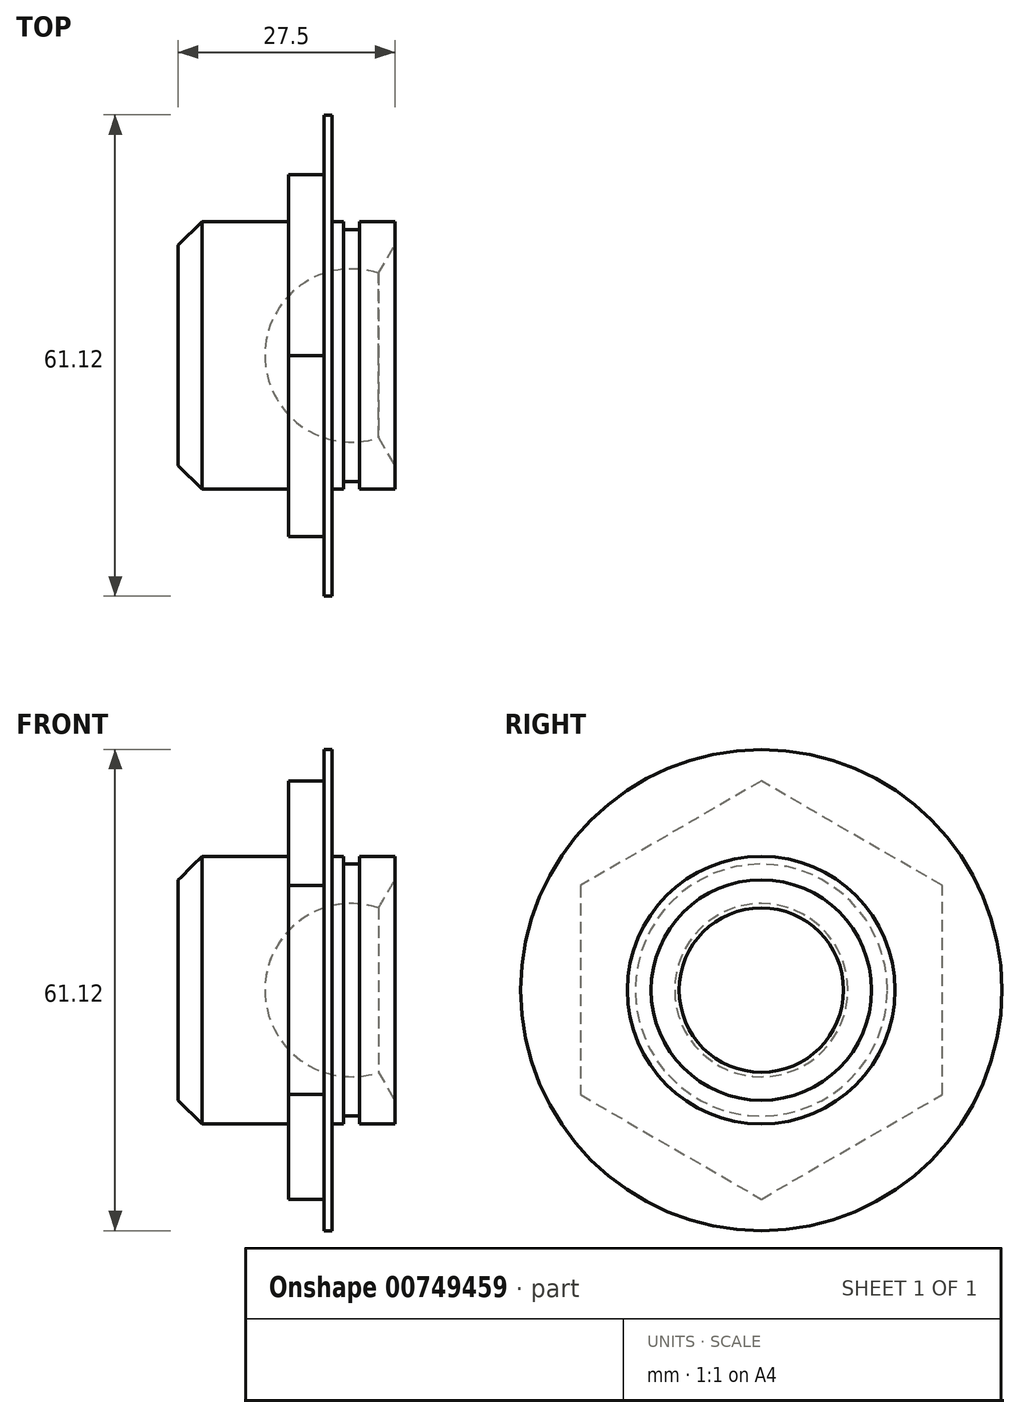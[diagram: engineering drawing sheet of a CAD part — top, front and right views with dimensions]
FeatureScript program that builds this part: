
annotation { "Feature Type Name" : "Feature", "Feature Type Description" : "" }
export const myFeature = defineFeature(function(context is Context, id is Id, definition is map)
    precondition{}
    {
        {
            var Q0;
            Q0=qCreatedBy(makeId("Front.planeOp"),FACE);
            var sketch = newSketch(context, id + "F0", { "sketchPlane" : qUnion([Q0])});
            skLineSegment(sketch, "E0", {"start": v(0, 0) * mm, "end": v(22, 0) * mm, "construction": true});
            skLineSegment(sketch, "E1", {"start": v(0, 0) * mm, "end": v(0, 17) * mm});
            skLineSegment(sketch, "E2", {"start": v(0, 17) * mm, "end": v(14, 17) * mm});
            skLineSegment(sketch, "E3", {"start": v(14, 17) * mm, "end": v(14, 40) * mm});
            skLineSegment(sketch, "E4", {"start": v(14, 40) * mm, "end": v(18.5, 40) * mm});
            skLineSegment(sketch, "E5", {"start": v(18.5, 40) * mm, "end": v(18.5, 17) * mm});
            skLineSegment(sketch, "E6", {"start": v(18.5, 17) * mm, "end": v(21, 17) * mm});
            skArc(sketch, "E7", {"start": v(25.45, 10.45) * mm, "mid": v(15.56, 8.91) * mm, "end": v(11, 0) * mm});
            skLineSegment(sketch, "E8", {"start": v(25.45, 10.45) * mm, "end": v(27.5, 14) * mm});
            skLineSegment(sketch, "E9", {"start": v(27.5, 17) * mm, "end": v(27.5, 14) * mm});
            skLineSegment(sketch, "E10", {"start": v(0, 0) * mm, "end": v(11, 0) * mm});
            skLineSegment(sketch, "E11", {"start": v(23, 17) * mm, "end": v(23, 16) * mm});
            skLineSegment(sketch, "E12", {"start": v(23, 16) * mm, "end": v(21, 16) * mm});
            skLineSegment(sketch, "E13", {"start": v(21, 16) * mm, "end": v(21, 17) * mm});
            skLineSegment(sketch, "E14.trimOffspring", {"start": v(23, 17) * mm, "end": v(27.5, 17) * mm});
            skSolve(sketch);
        }
        {
            var Q0;
            Q0=makeQuery(id+"F0.imprint","IMPRINT",FACE,{"disambiguationData":[TD([[makeQuery(id+"F0.imprint","IMPRINT",EDGE,{"derivedFrom":sQuery(id+"F0.wireOp",EDGE,"E1")}),-1.0]])]});
            var Q1;
            Q1=sQuery(id+"F0.wireOp",EDGE,"E0");
            revolve(context, id + "F1", {"surfaceOperationType" : NewSurfaceOperationType.NEW, "entities" : qUnion([Q0]), "axis" : qUnion([Q1]), "revolveType" : RevolveType.FULL});
        }
        {
            var Q0;
            Q0=makeQuery(id+"F1.opRevolve","SWEPT_FACE",FACE,{"disambiguationData":[OSD([sQuery(id+"F0.wireOp",EDGE,"E3")])]});
            var sketch = newSketch(context, id + "F2", { "sketchPlane" : qUnion([Q0])});
            skLineSegment(sketch, "E15.bottom", {"start": v(23, -47.62) * mm, "end": v(64.72, -47.62) * mm});
            skLineSegment(sketch, "E15.top", {"start": v(23, 47.62) * mm, "end": v(64.72, 47.62) * mm});
            skLineSegment(sketch, "E15.left", {"start": v(23, -47.62) * mm, "end": v(23, 47.62) * mm});
            skLineSegment(sketch, "E15.right", {"start": v(64.72, -47.62) * mm, "end": v(64.72, 47.62) * mm});
            skPoint(sketch, "E15.middle", {"position": v(43.86, 0) * mm});
            skLineSegment(sketch, "E16.1.0", {"start": v(52.74, -3.89) * mm, "end": v(73.6, 32.24) * mm});
            skLineSegment(sketch, "E16.1.1", {"start": v(52.74, -3.89) * mm, "end": v(-29.74, 43.73) * mm});
            skLineSegment(sketch, "E16.1.2", {"start": v(-29.74, 43.73) * mm, "end": v(-8.88, 79.86) * mm});
            skLineSegment(sketch, "E16.1.3", {"start": v(73.6, 32.24) * mm, "end": v(-8.88, 79.86) * mm});
            skLineSegment(sketch, "E16.2.0", {"start": v(29.74, 43.73) * mm, "end": v(8.88, 79.86) * mm});
            skLineSegment(sketch, "E16.2.1", {"start": v(29.74, 43.73) * mm, "end": v(-52.74, -3.89) * mm});
            skLineSegment(sketch, "E16.2.2", {"start": v(-52.74, -3.89) * mm, "end": v(-73.6, 32.24) * mm});
            skLineSegment(sketch, "E16.2.3", {"start": v(8.88, 79.86) * mm, "end": v(-73.6, 32.24) * mm});
            skLineSegment(sketch, "E16.3.0", {"start": v(-23, 47.62) * mm, "end": v(-64.72, 47.62) * mm});
            skLineSegment(sketch, "E16.3.1", {"start": v(-23, 47.62) * mm, "end": v(-23, -47.62) * mm});
            skLineSegment(sketch, "E16.3.2", {"start": v(-23, -47.62) * mm, "end": v(-64.72, -47.62) * mm});
            skLineSegment(sketch, "E16.3.3", {"start": v(-64.72, 47.62) * mm, "end": v(-64.72, -47.62) * mm});
            skLineSegment(sketch, "E16.4.0", {"start": v(-52.74, 3.89) * mm, "end": v(-73.6, -32.24) * mm});
            skLineSegment(sketch, "E16.4.1", {"start": v(-52.74, 3.89) * mm, "end": v(29.74, -43.73) * mm});
            skLineSegment(sketch, "E16.4.2", {"start": v(29.74, -43.73) * mm, "end": v(8.88, -79.86) * mm});
            skLineSegment(sketch, "E16.4.3", {"start": v(-73.6, -32.24) * mm, "end": v(8.88, -79.86) * mm});
            skLineSegment(sketch, "E16.5.0", {"start": v(-29.74, -43.73) * mm, "end": v(-8.88, -79.86) * mm});
            skLineSegment(sketch, "E16.5.1", {"start": v(-29.74, -43.73) * mm, "end": v(52.74, 3.89) * mm});
            skLineSegment(sketch, "E16.5.2", {"start": v(52.74, 3.89) * mm, "end": v(73.6, -32.24) * mm});
            skLineSegment(sketch, "E16.5.3", {"start": v(-8.88, -79.86) * mm, "end": v(73.6, -32.24) * mm});
            skPoint(sketch, "E16.center", {"position": v(0, 0) * mm});
            skSolve(sketch);
        }
        {
            var Q0;
            {var subQ0=sQuery(id+"F2.wireOp",EDGE,"E16.5.1");var subQ1=sQuery(id+"F2.wireOp",EDGE,"E15.left");var subQ2=makeQuery(id+"F2.imprint","INTERSECT",VERTEX,{"derivedFrom":[subQ1,subQ0]});Q0=makeQuery(id+"F2.imprint","IMPRINT",FACE,{"disambiguationData":[TD([[makeQuery(id+"F2.imprint","IMPRINT",EDGE,{"disambiguationData":[TD([[subQ2,1.0]])],"derivedFrom":subQ0}),-1.0]])]});}
            var Q1;
            {var subQ0=sQuery(id+"F2.wireOp",EDGE,"E16.5.1");var subQ1=sQuery(id+"F2.wireOp",EDGE,"E15.left");var subQ2=makeQuery(id+"F2.imprint","INTERSECT",VERTEX,{"derivedFrom":[subQ1,subQ0]});Q1=makeQuery(id+"F2.imprint","IMPRINT",FACE,{"disambiguationData":[TD([[makeQuery(id+"F2.imprint","IMPRINT",EDGE,{"disambiguationData":[TD([[subQ2,1.0]])],"derivedFrom":subQ1}),-1.0]])]});}
            var Q2;
            {var subQ0=sQuery(id+"F2.wireOp",EDGE,"E16.5.1");var subQ1=sQuery(id+"F2.wireOp",EDGE,"E15.left");var subQ2=makeQuery(id+"F2.imprint","INTERSECT",VERTEX,{"derivedFrom":[subQ1,subQ0]});Q2=makeQuery(id+"F2.imprint","IMPRINT",FACE,{"disambiguationData":[TD([[makeQuery(id+"F2.imprint","IMPRINT",EDGE,{"disambiguationData":[TD([[subQ2,-1.0]])],"derivedFrom":subQ1}),-1.0]])]});}
            var Q3;
            {var subQ0=sQuery(id+"F2.wireOp",EDGE,"E16.1.1");var subQ1=sQuery(id+"F2.wireOp",EDGE,"E15.left");var subQ2=makeQuery(id+"F2.imprint","INTERSECT",VERTEX,{"derivedFrom":[subQ1,subQ0]});Q3=makeQuery(id+"F2.imprint","IMPRINT",FACE,{"disambiguationData":[TD([[makeQuery(id+"F2.imprint","IMPRINT",EDGE,{"disambiguationData":[TD([[subQ2,-1.0]])],"derivedFrom":subQ1}),-1.0]])]});}
            var Q4;
            {var subQ0=sQuery(id+"F2.wireOp",EDGE,"E16.1.1");var subQ1=sQuery(id+"F2.wireOp",EDGE,"E15.left");var subQ2=makeQuery(id+"F2.imprint","INTERSECT",VERTEX,{"derivedFrom":[subQ1,subQ0]});Q4=makeQuery(id+"F2.imprint","IMPRINT",FACE,{"disambiguationData":[TD([[makeQuery(id+"F2.imprint","IMPRINT",EDGE,{"disambiguationData":[TD([[subQ2,-1.0]])],"derivedFrom":subQ0}),-1.0]])]});}
            var Q5;
            {var subQ0=sQuery(id+"F2.wireOp",EDGE,"E16.2.1");var subQ1=sQuery(id+"F2.wireOp",EDGE,"E16.1.1");var subQ2=makeQuery(id+"F2.imprint","INTERSECT",VERTEX,{"derivedFrom":[subQ1,subQ0]});Q5=makeQuery(id+"F2.imprint","IMPRINT",FACE,{"disambiguationData":[TD([[makeQuery(id+"F2.imprint","IMPRINT",EDGE,{"disambiguationData":[TD([[subQ2,-1.0]])],"derivedFrom":subQ1}),-1.0]])]});}
            var Q6;
            {var subQ0=sQuery(id+"F2.wireOp",EDGE,"E16.2.1");var subQ1=sQuery(id+"F2.wireOp",EDGE,"E16.1.1");var subQ2=makeQuery(id+"F2.imprint","INTERSECT",VERTEX,{"derivedFrom":[subQ1,subQ0]});Q6=makeQuery(id+"F2.imprint","IMPRINT",FACE,{"disambiguationData":[TD([[makeQuery(id+"F2.imprint","IMPRINT",EDGE,{"disambiguationData":[TD([[subQ2,-1.0]])],"derivedFrom":subQ0}),-1.0]])]});}
            var Q7;
            {var subQ0=sQuery(id+"F2.wireOp",EDGE,"E16.3.1");var subQ1=sQuery(id+"F2.wireOp",EDGE,"E16.2.1");var subQ2=makeQuery(id+"F2.imprint","INTERSECT",VERTEX,{"derivedFrom":[subQ1,subQ0]});Q7=makeQuery(id+"F2.imprint","IMPRINT",FACE,{"disambiguationData":[TD([[makeQuery(id+"F2.imprint","IMPRINT",EDGE,{"disambiguationData":[TD([[subQ2,-1.0]])],"derivedFrom":subQ0}),-1.0]])]});}
            var Q8;
            {var subQ0=sQuery(id+"F2.wireOp",EDGE,"E16.4.1");var subQ1=sQuery(id+"F2.wireOp",EDGE,"E16.3.1");var subQ2=makeQuery(id+"F2.imprint","INTERSECT",VERTEX,{"derivedFrom":[subQ1,subQ0]});Q8=makeQuery(id+"F2.imprint","IMPRINT",FACE,{"disambiguationData":[TD([[makeQuery(id+"F2.imprint","IMPRINT",EDGE,{"disambiguationData":[TD([[subQ2,-1.0]])],"derivedFrom":subQ1}),-1.0]])]});}
            var Q9;
            {var subQ0=sQuery(id+"F2.wireOp",EDGE,"E16.4.1");var subQ1=sQuery(id+"F2.wireOp",EDGE,"E16.3.1");var subQ2=makeQuery(id+"F2.imprint","INTERSECT",VERTEX,{"derivedFrom":[subQ1,subQ0]});Q9=makeQuery(id+"F2.imprint","IMPRINT",FACE,{"disambiguationData":[TD([[makeQuery(id+"F2.imprint","IMPRINT",EDGE,{"disambiguationData":[TD([[subQ2,-1.0]])],"derivedFrom":subQ0}),-1.0]])]});}
            var Q10;
            {var subQ0=sQuery(id+"F2.wireOp",EDGE,"E16.5.1");var subQ1=sQuery(id+"F2.wireOp",EDGE,"E16.4.1");var subQ2=makeQuery(id+"F2.imprint","INTERSECT",VERTEX,{"derivedFrom":[subQ1,subQ0]});Q10=makeQuery(id+"F2.imprint","IMPRINT",FACE,{"disambiguationData":[TD([[makeQuery(id+"F2.imprint","IMPRINT",EDGE,{"disambiguationData":[TD([[subQ2,-1.0]])],"derivedFrom":subQ1}),-1.0]])]});}
            var Q11;
            {var subQ0=sQuery(id+"F2.wireOp",EDGE,"E16.3.1");var subQ1=sQuery(id+"F2.wireOp",EDGE,"E16.2.1");var subQ2=makeQuery(id+"F2.imprint","INTERSECT",VERTEX,{"derivedFrom":[subQ1,subQ0]});Q11=makeQuery(id+"F2.imprint","IMPRINT",FACE,{"disambiguationData":[TD([[makeQuery(id+"F2.imprint","IMPRINT",EDGE,{"disambiguationData":[TD([[subQ2,-1.0]])],"derivedFrom":subQ1}),-1.0]])]});}
            extrude(context, id + "F3", {"entities" : qUnion([Q0, Q1, Q2, Q3, Q4, Q5, Q6, Q7, Q8, Q9, Q10, Q11]), "operationType" : NewBodyOperationType.REMOVE, "oppositeDirection" : true, "depth" : 25 * mm, "offsetDistance" : 25 * mm});
        }
        {
            var Q0;
            Q0=makeQuery(id+"F1.opRevolve","SWEPT_EDGE",EDGE,{"disambiguationData":[OSD([sQuery(id+"F0.wireOp",EDGE,"E1"),sQuery(id+"F0.wireOp",EDGE,"E2")])]});
            chamfer(context, id + "F4", {"entities" : qUnion([Q0]), "width" : 3 * mm, "tangentPropagation" : true});
        }
        {
            var Q0;
            Q0=makeQuery(id+"F1.opRevolve","SWEPT_FACE",FACE,{"disambiguationData":[OSD([sQuery(id+"F0.wireOp",EDGE,"E5")])]});
            var sketch = newSketch(context, id + "F5", { "sketchPlane" : qUnion([Q0])});
            skCircle(sketch, "E17", {"center": v(0, 0) * mm, "radius": 30.56 * mm});
            skSolve(sketch);
        }
        {
            var Q0;
            {var subQ0=sQuery(id+"F0.wireOp",EDGE,"E5");Q0=makeQuery(id+"F5.imprint","IMPRINT",FACE,{"disambiguationData":[TD([[makeQuery(id+"F5.imprint","IMPRINT",EDGE,{"derivedFrom":makeQuery(id+"F1.opRevolve","SWEPT_EDGE",EDGE,{"disambiguationData":[OSD([subQ0,sQuery(id+"F0.wireOp",EDGE,"E6")])]})}),1.0]])]});}
            var Q1;
            Q1=makeQuery(id+"F5.imprint","IMPRINT",FACE,{"disambiguationData":[TD([[makeQuery(id+"F5.imprint","IMPRINT",EDGE,{"derivedFrom":sQuery(id+"F5.wireOp",EDGE,"E17")}),1.0]])]});
            extrude(context, id + "F6", {"entities" : qUnion([Q0, Q1]), "operationType" : NewBodyOperationType.ADD, "depth" : 1 * mm, "offsetDistance" : 25 * mm});
        }
    });
